# Revit family: Bathroom_Accessory-Robe_Hook-Kohler-Kelston-13505
name_source: partatom
category: Specialty Equipment
units: mm (PartAtom-declared; Revit-internal decimal feet)

## family parameters
Cut with Voids When Loaded = No
Host = Face
OmniClass Number = 23.40.20.21.31
OmniClass Title = Robe Hooks
Part Type = Normal
Room Calculation Point = No
Round Connector Dimension = Use Diameter
Shared = No

## types (1)
- Nickel-Vibrant_Brushed_Nickel-BN
    Assembly Code = C1030200
    Default Elevation = 0' - 0"
    Description = Kelston(TM) robe hook
    Finish = Nickel-Kohler-BN-Vibrant_Brushed_Nickel
    Height = 0' - 4 15/16"
    Length = 0' - 5 5/16"
    Manufacturer = Kohler
    Model = K-13505
    Product Documentation Link = http://www.us.kohler.com
    Product Page URL = http://www.us.kohler.com
    Product data url = https://bimobject.com
    URL = http://www.us.kohler.com
    Width = 0' - 2 7/16"

## geometry (parser evidence)
native form markers: Sweep x5
no freeform markers — native parametric forms only
